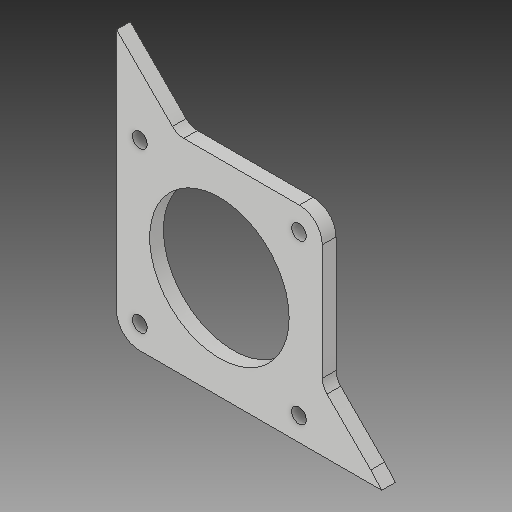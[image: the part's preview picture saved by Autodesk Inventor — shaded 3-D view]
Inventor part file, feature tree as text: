
AUTODESK INVENTOR PART (.ipt)
format: ipt  version: 2018 (Build 220112000, 112)  size: 147,456 bytes
history: native  units: mm
features: extrude x4, sketch x4, reference x4, fillet x1
ambient origin geometry x8: Origin, YZ Plane, XZ Plane, XY Plane, X Axis, Y Axis, Z Axis, Center Point
bodies: Solid1 (feature_tree)
feature tree (13):
  extrude  "Extrusion1"  Depth=90.0mm
  extrude  "Extrusion2"  Depth=6.0mm TaperAngle=0.0deg
  extrude  "Extrusion3"  Depth=6.0mm TaperAngle=0.0deg
  fillet  "Fillet1"  Radius=6.0mm
  extrude  "Extrusion4"  Depth=7.0mm
  sketch  "Sketch1"  dims[d0=90.0mm d1=90.0mm]
  sketch  "Sketch2"  dims[d2=10.0mm d3=6.0mm d4=0.0mm]
  sketch  "Sketch3"  dims[d5=61.0mm d6=6.0mm d7=0.0mm d9=6.0mm d10=0.0mm]
  sketch  "Sketch4"  dims[d13=53.5mm d15=7.0mm d16=10.0mm d17=0.0mm]
  reference  "Reference1"
  reference  "Reference2"
  reference  "Reference3"
  reference  "Reference4"
